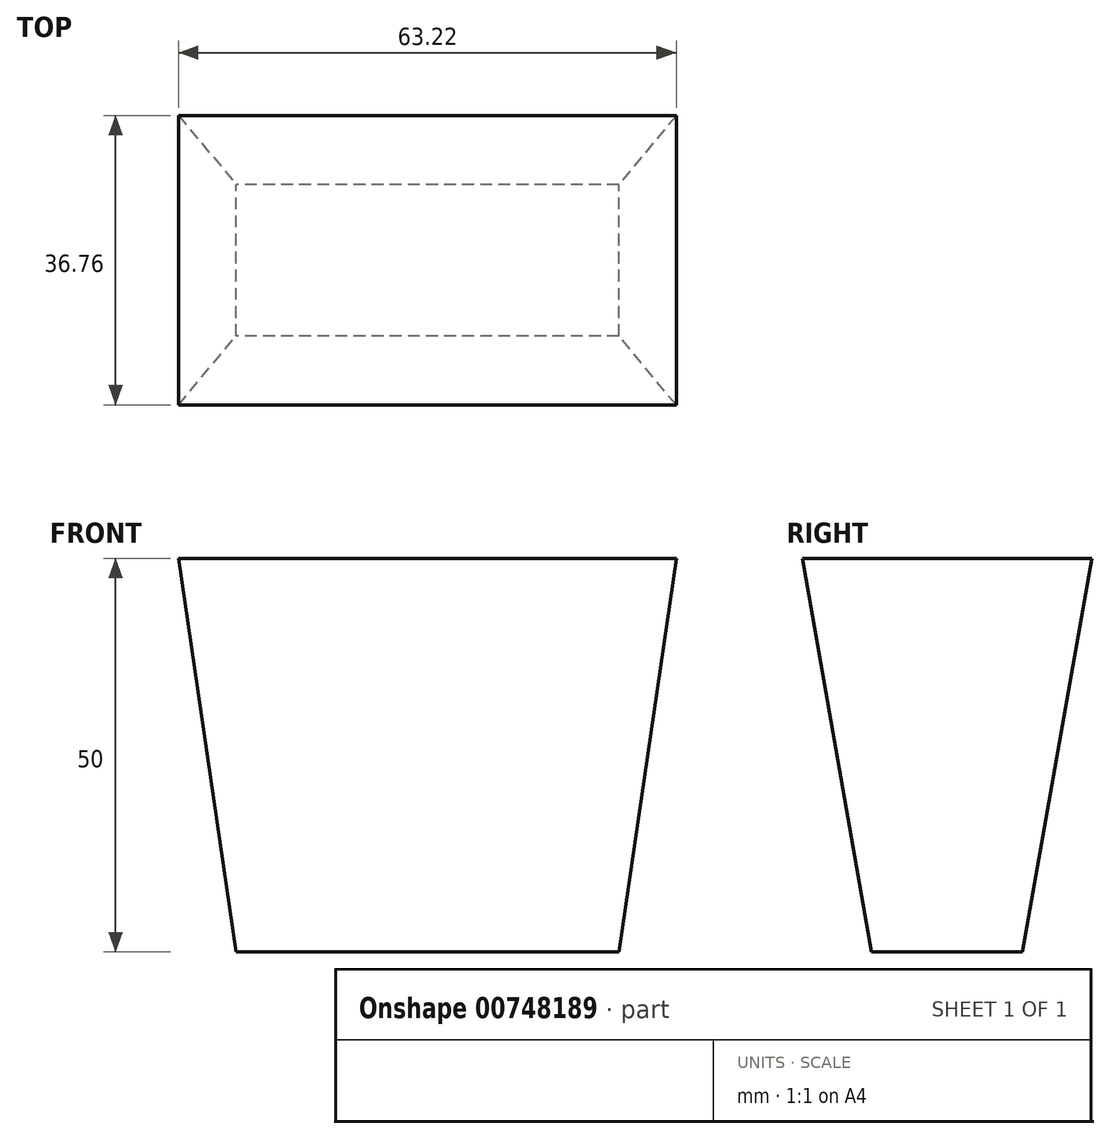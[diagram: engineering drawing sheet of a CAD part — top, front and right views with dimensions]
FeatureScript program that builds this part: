
annotation { "Feature Type Name" : "Feature", "Feature Type Description" : "" }
export const myFeature = defineFeature(function(context is Context, id is Id, definition is map)
    precondition{}
    {
        {
            var Q0;
            Q0=qCreatedBy(makeId("Top.planeOp"),FACE);
            var sketch = newSketch(context, id + "F0", { "sketchPlane" : qUnion([Q0])});
            skLineSegment(sketch, "E0.bottom", {"start": v(24.31, -9.62) * mm, "end": v(-24.31, -9.62) * mm});
            skLineSegment(sketch, "E0.top", {"start": v(24.31, 9.62) * mm, "end": v(-24.31, 9.62) * mm});
            skLineSegment(sketch, "E0.left", {"start": v(24.31, -9.62) * mm, "end": v(24.31, 9.62) * mm});
            skLineSegment(sketch, "E0.right", {"start": v(-24.31, -9.62) * mm, "end": v(-24.31, 9.62) * mm});
            skPoint(sketch, "E0.middle", {"position": v(0, 0) * mm});
            skSolve(sketch);
        }
        {
            var Q0;
            Q0=qCreatedBy(makeId("Top.planeOp"),FACE);
            cPlane(context, id + "F1", {"entities" : qUnion([Q0]), "cplaneType" : CPlaneType.OFFSET, "offset" : 50 * mm, "width" : 150 * mm, "height" : 150 * mm});
        }
        {
            var Q0;
            Q0=qCreatedBy(id+"F1.planeOp",FACE);
            var sketch = newSketch(context, id + "F2", { "sketchPlane" : qUnion([Q0])});
            skLineSegment(sketch, "E1.bottom", {"start": v(31.6, -18.38) * mm, "end": v(-31.6, -18.38) * mm});
            skLineSegment(sketch, "E1.top", {"start": v(31.6, 18.38) * mm, "end": v(-31.6, 18.38) * mm});
            skLineSegment(sketch, "E1.left", {"start": v(31.6, -18.38) * mm, "end": v(31.6, 18.38) * mm});
            skLineSegment(sketch, "E1.right", {"start": v(-31.6, -18.38) * mm, "end": v(-31.6, 18.38) * mm});
            skPoint(sketch, "E1.middle", {"position": v(0, 0) * mm});
            skSolve(sketch);
        }
        {
            var Q0;
            Q0=makeQuery(id+"F2.imprint","IMPRINT",FACE,{"disambiguationData":[TD([[makeQuery(id+"F2.imprint","IMPRINT",EDGE,{"derivedFrom":sQuery(id+"F2.wireOp",EDGE,"E1.bottom")}),-1.0]])]});
            var Q1;
            Q1=makeQuery(id+"F0.imprint","IMPRINT",FACE,{"disambiguationData":[TD([[makeQuery(id+"F0.imprint","IMPRINT",EDGE,{"derivedFrom":sQuery(id+"F0.wireOp",EDGE,"E0.bottom")}),-1.0]])]});
            loft(context, id + "F3", {"sheetProfilesArray" : [{ "sheetProfileEntities" : qUnion([Q0]) }, { "sheetProfileEntities" : qUnion([Q1]) }]});
        }
    });
